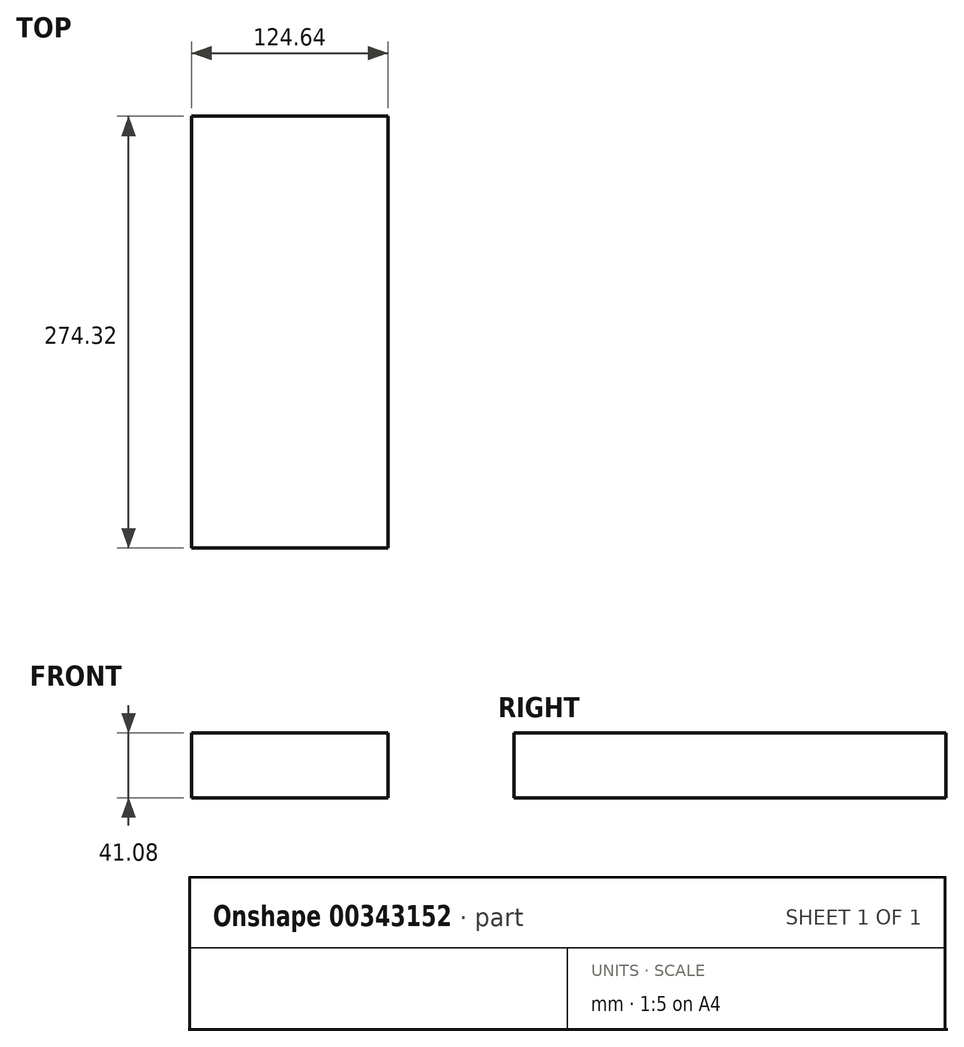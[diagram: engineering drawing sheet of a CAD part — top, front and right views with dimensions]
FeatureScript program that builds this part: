
annotation { "Feature Type Name" : "Feature", "Feature Type Description" : "" }
export const myFeature = defineFeature(function(context is Context, id is Id, definition is map)
    precondition{}
    {
        {
            var Q0;
            Q0=qCreatedBy(makeId("Front.planeOp"),FACE);
            var sketch = newSketch(context, id + "F0", { "sketchPlane" : qUnion([Q0])});
            skLineSegment(sketch, "E0.bottom", {"start": v(62.32, 20.54) * mm, "end": v(-62.32, 20.54) * mm});
            skLineSegment(sketch, "E0.top", {"start": v(62.32, -20.54) * mm, "end": v(-62.32, -20.54) * mm});
            skLineSegment(sketch, "E0.left", {"start": v(62.32, 20.54) * mm, "end": v(62.32, -20.54) * mm});
            skLineSegment(sketch, "E0.right", {"start": v(-62.32, 20.54) * mm, "end": v(-62.32, -20.54) * mm});
            skPoint(sketch, "E0.middle", {"position": v(0, 0) * mm});
            skSolve(sketch);
        }
        {
            var Q0;
            Q0=makeQuery(id+"F0.imprint","IMPRINT",FACE,{"disambiguationData":[TD([[makeQuery(id+"F0.imprint","IMPRINT",EDGE,{"derivedFrom":sQuery(id+"F0.wireOp",EDGE,"E0.bottom")}),1.0]])]});
            extrude(context, id + "F1", {"entities" : qUnion([Q0]), "depth" : 274.32 * mm});
        }
    });
